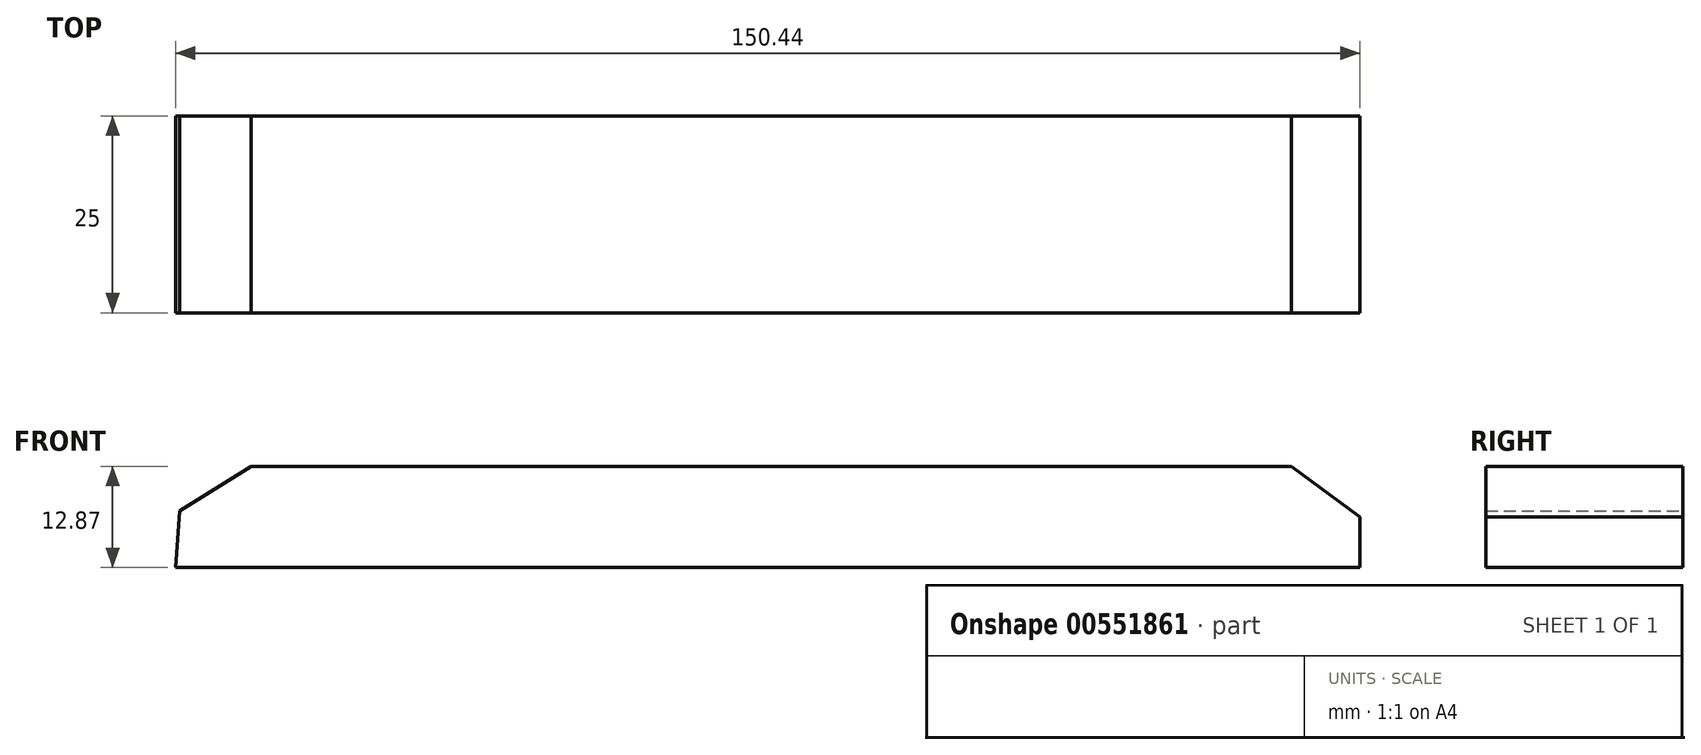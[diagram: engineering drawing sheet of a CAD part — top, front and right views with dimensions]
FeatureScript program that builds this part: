
annotation { "Feature Type Name" : "Feature", "Feature Type Description" : "" }
export const myFeature = defineFeature(function(context is Context, id is Id, definition is map)
    precondition{}
    {
        {
            var Q0;
            Q0=qCreatedBy(makeId("Front.planeOp"),FACE);
            var sketch = newSketch(context, id + "F0", { "sketchPlane" : qUnion([Q0])});
            skLineSegment(sketch, "E0", {"start": v(-75.85, 0) * mm, "end": v(74.59, 0) * mm});
            skLineSegment(sketch, "E1", {"start": v(74.59, 0) * mm, "end": v(74.59, 6.44) * mm});
            skLineSegment(sketch, "E2", {"start": v(74.59, 6.44) * mm, "end": v(65.88, 12.87) * mm});
            skLineSegment(sketch, "E3", {"start": v(65.88, 12.87) * mm, "end": v(-66.26, 12.87) * mm});
            skLineSegment(sketch, "E4", {"start": v(-66.26, 12.87) * mm, "end": v(-75.34, 7.2) * mm});
            skLineSegment(sketch, "E5", {"start": v(-75.34, 7.2) * mm, "end": v(-75.85, 0) * mm});
            skSolve(sketch);
        }
        {
            var Q0;
            Q0=makeQuery(id+"F0.imprint","IMPRINT",FACE,{"disambiguationData":[TD([[makeQuery(id+"F0.imprint","IMPRINT",EDGE,{"derivedFrom":sQuery(id+"F0.wireOp",EDGE,"E0")}),1.0]])]});
            extrude(context, id + "F1", {"entities" : qUnion([Q0]), "depth" : 25 * mm, "offsetDistance" : 25 * mm});
        }
    });
